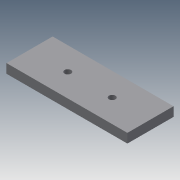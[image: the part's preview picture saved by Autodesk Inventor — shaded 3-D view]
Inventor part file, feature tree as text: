
AUTODESK INVENTOR PART (.ipt)
format: ipt  version: 2013 (Build 170138000, 138)  size: 75,264 bytes
history: native  units: mm
features: extrude x1, sketch x1
ambient origin geometry x8: Origin, YZ Plane, XZ Plane, XY Plane, X Axis, Y Axis, Z Axis, Center Point
bodies: Solid1 (feature_tree)
feature tree (2):
  extrude  "Extrusion1"  Depth=50.0mm
  sketch  "Sketch1"  dims[d0=131.0mm d1=50.0mm d2=24.1mm d3=24.1mm d4=7.0mm d5=7.0mm d6=10.0mm d7=0.0mm]
